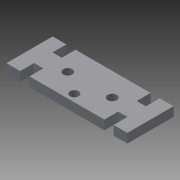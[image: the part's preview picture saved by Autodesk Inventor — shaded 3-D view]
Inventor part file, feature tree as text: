
AUTODESK INVENTOR PART (.ipt)
format: ipt  version: 2015 (Build 190159000, 159)  size: 135,680 bytes
history: native  units: mm
features: sketch x3, extrude x3, plane x1, fillet x1
ambient origin geometry x8: Origin, YZ Plane, XZ Plane, XY Plane, X Axis, Y Axis, Z Axis, Center Point
bodies: Body1 (feature_tree)
feature tree (8):
  sketch  "Sketch1"  dims[d0=15.0mm d1=15.0mm d2=15.0mm d3=15.0mm d8=15.0mm]
  plane  "Work Plane1"
  sketch  "Sketch2"  dims[d9=15.0mm d20=2.5mm]
  extrude  "Extrusion11"  Depth=15.0mm
  extrude  "Extrusion12"  Depth=15.0mm
  extrude  "Extrusion14"  Depth=9.5mm
  fillet  "Fillet1"  Radius=10.0mm
  sketch  "Sketch4"  dims[d23=8.0mm d24=9.5mm d27=10.0mm d28=10.0mm d39=10.0mm d40=0.0mm d41=8.0mm d42=0.0mm d50=5.0mm d51=2.5mm d52=10.0mm d53=0.0mm d54=2.0mm]
